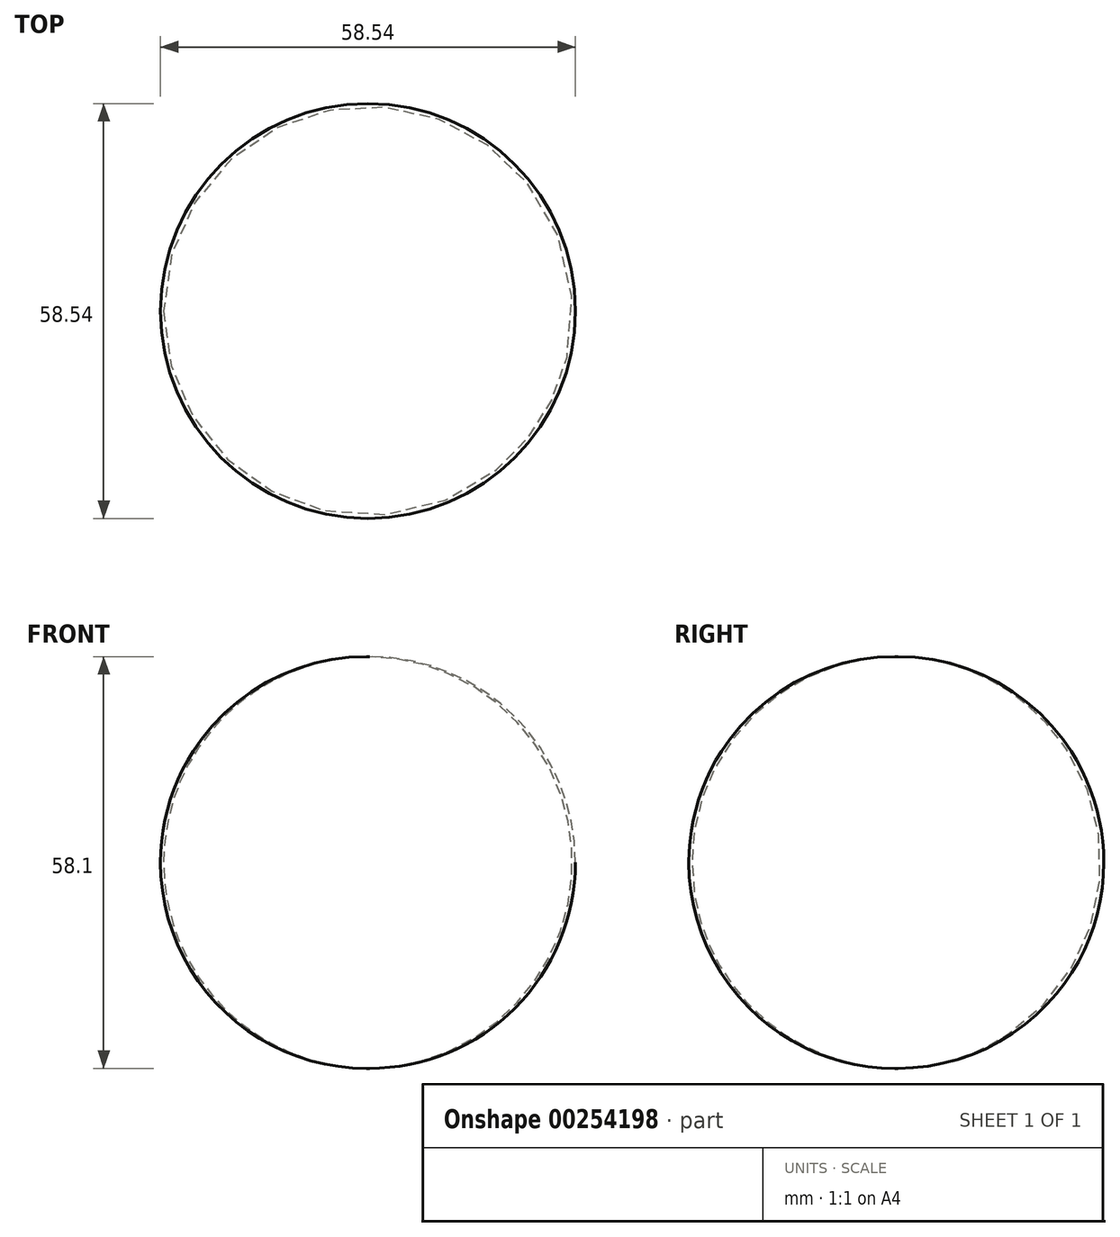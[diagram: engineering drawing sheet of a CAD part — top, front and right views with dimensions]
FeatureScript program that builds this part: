
annotation { "Feature Type Name" : "Feature", "Feature Type Description" : "" }
export const myFeature = defineFeature(function(context is Context, id is Id, definition is map)
    precondition{}
    {
        {
            var Q0;
            Q0=qCreatedBy(makeId("Front.planeOp"),FACE);
            var sketch = newSketch(context, id + "F0", { "sketchPlane" : qUnion([Q0])});
            skLineSegment(sketch, "E0", {"start": v(0, 0) * mm, "end": v(0, 57.6) * mm});
            skSolve(sketch);
        }
        {
            var Q0;
            Q0=qCreatedBy(makeId("Front.planeOp"),FACE);
            var sketch = newSketch(context, id + "F1", { "sketchPlane" : qUnion([Q0])});
            skArc(sketch, "E1", {"start": v(0, 0) * mm, "mid": v(28.83, 29.05) * mm, "end": v(0, 58.1) * mm});
            skSolve(sketch);
        }
        {
            var Q0;
            Q0=sQuery(id+"F1.wireOp",EDGE,"E1");
            var Q1;
            Q1=sQuery(id+"F0.wireOp",EDGE,"E0");
            revolve(context, id + "F2", {"bodyType" : ToolBodyType.SURFACE, "surfaceEntities" : qUnion([Q0]), "axis" : qUnion([Q1]), "revolveType" : RevolveType.FULL});
        }
    });
